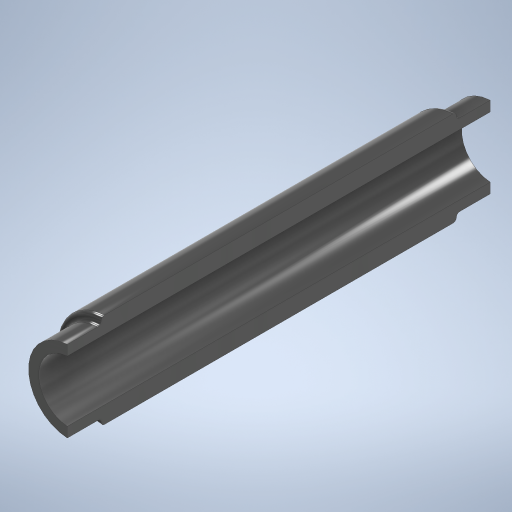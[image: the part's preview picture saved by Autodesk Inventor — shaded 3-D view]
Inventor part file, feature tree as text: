
AUTODESK INVENTOR PART (.ipt)
format: ipt  version: 2023.4 (Build 274418000, 418)  size: 288,768 bytes
history: native  units: mm
features: extrude x5, sketch x5, fillet x1
ambient origin geometry x8: Origin, YZ Plane, XZ Plane, XY Plane, X Axis, Y Axis, Z Axis, Center Point
bodies: Solid1 (feature_tree)
feature tree (11):
  extrude  "Extrusion1"  Depth=105.0mm TaperAngle=0.0deg
  extrude  "Extrusion2"  Depth=10.0mm TaperAngle=0.0deg
  extrude  "Extrusion3"  Depth=1.0mm
  fillet  "Fillet1"  Radius=3.0mm
  extrude  "Extrusion4"  Depth=10.0mm
  extrude  "Extrusion5"  [1 undecoded]
  sketch  "Sketch1"  dims[d0=28.0mm d1=105.0mm d2=0.0mm]
  sketch  "Sketch2"  dims[d3=2.0mm d4=10.0mm d5=0.0mm]
  sketch  "Sketch3"  dims[d6=10.0mm d7=0.0mm d8=1.0mm d9=3.0mm]
  sketch  "Sketch4"  dims[d10=10.0mm d11=0.0mm d12=0.55mm]
  sketch  "Sketch5"  dims[d13=0.0mm d14=0.0mm]
note: 1 required parameter value undecoded (feature->parameter linkage not recoverable at this tier; creation-order binding heuristic only, values carry confidence <= 0.55)
